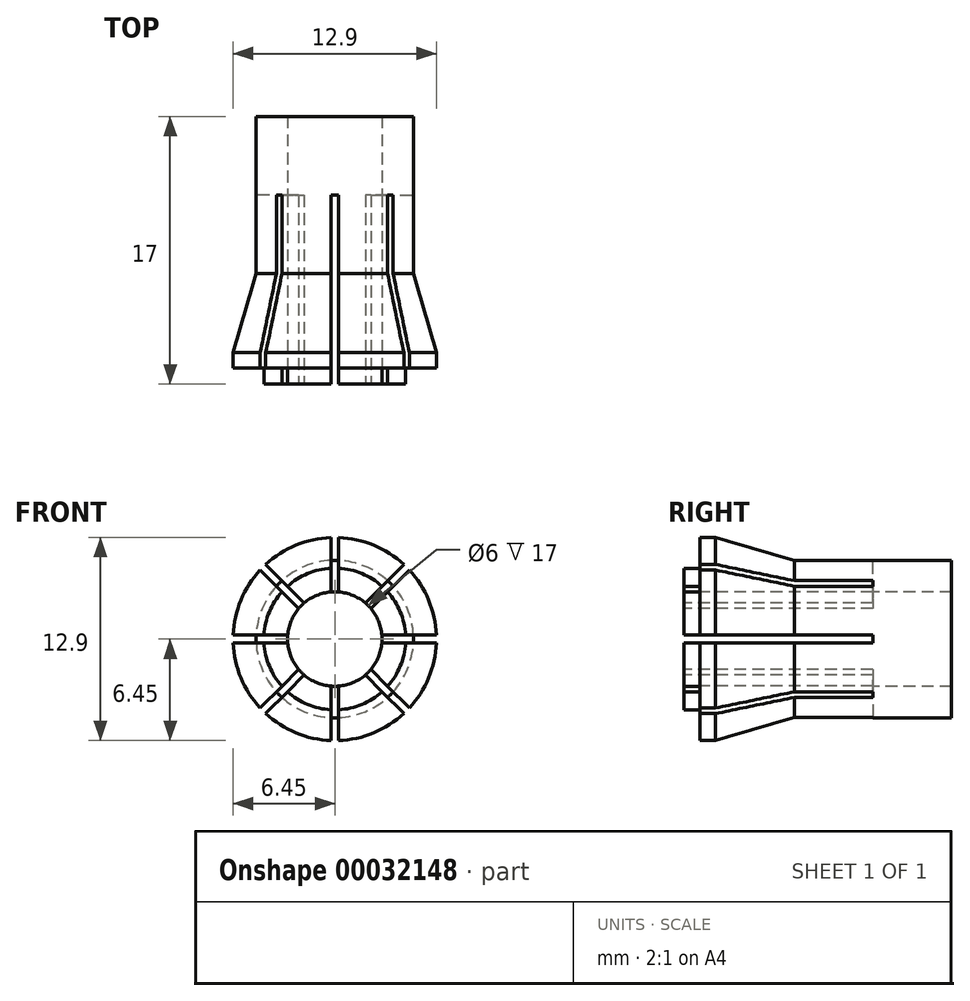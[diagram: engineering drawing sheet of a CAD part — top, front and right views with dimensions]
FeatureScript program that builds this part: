
annotation { "Feature Type Name" : "Feature", "Feature Type Description" : "" }
export const myFeature = defineFeature(function(context is Context, id is Id, definition is map)
    precondition{}
    {
        {
            var Q0;
            Q0=qCreatedBy(makeId("Right.planeOp"),FACE);
            var sketch = newSketch(context, id + "F0", { "sketchPlane" : qUnion([Q0])});
            skLineSegment(sketch, "E0", {"start": v(0, 5) * mm, "end": v(-10, 5) * mm});
            skLineSegment(sketch, "E1", {"start": v(-10, 5) * mm, "end": v(-15, 6.45) * mm});
            skLineSegment(sketch, "E2", {"start": v(-15, 6.45) * mm, "end": v(-16, 6.45) * mm});
            skLineSegment(sketch, "E3", {"start": v(-16, 6.45) * mm, "end": v(-16, 4.5) * mm});
            skLineSegment(sketch, "E4", {"start": v(-16, 4.5) * mm, "end": v(-17, 4.5) * mm});
            skLineSegment(sketch, "E5", {"start": v(-17, 4.5) * mm, "end": v(-17, 3) * mm});
            skLineSegment(sketch, "E6", {"start": v(-17, 0) * mm, "end": v(0, 0) * mm});
            skLineSegment(sketch, "E7.0", {"start": v(-17, 3) * mm, "end": v(0, 3) * mm});
            skLineSegment(sketch, "E8", {"start": v(0, 5) * mm, "end": v(0, 3) * mm});
            skPoint(sketch, "E9.orphan", {"position": v(-23.9, 0) * mm});
            skSolve(sketch);
        }
        {
            var Q0;
            Q0 = qSketchRegion(id + "F0", true);
            var Q1;
            Q1=sQuery(id+"F0.wireOp",EDGE,"E6");
            revolve(context, id + "F1", {"entities" : qUnion([Q0]), "axis" : qUnion([Q1]), "revolveType" : RevolveType.FULL});
        }
        {
            var Q0;
            Q0=makeQuery(id+"F1.opRevolve","SWEPT_FACE",FACE,{"disambiguationData":[OSD([sQuery(id+"F0.wireOp",EDGE,"E5")])]});
            var sketch = newSketch(context, id + "F2", { "sketchPlane" : qUnion([Q0])});
            skLineSegment(sketch, "E10", {"start": v(-0.25, 0) * mm, "end": v(-0.25, 6.5) * mm});
            skLineSegment(sketch, "E11", {"start": v(-0.25, 6.5) * mm, "end": v(0.25, 6.5) * mm});
            skLineSegment(sketch, "E12", {"start": v(0.25, 6.5) * mm, "end": v(0.25, 0) * mm});
            skLineSegment(sketch, "E13", {"start": v(-0.25, 0) * mm, "end": v(0.25, 0) * mm});
            skLineSegment(sketch, "E14.1.0", {"start": v(-0.18, -0.18) * mm, "end": v(-4.77, 4.42) * mm});
            skLineSegment(sketch, "E14.1.1", {"start": v(-4.42, 4.77) * mm, "end": v(0.18, 0.18) * mm});
            skLineSegment(sketch, "E14.1.2", {"start": v(-4.77, 4.42) * mm, "end": v(-4.42, 4.77) * mm});
            skLineSegment(sketch, "E14.1.3", {"start": v(-0.18, -0.18) * mm, "end": v(0.18, 0.18) * mm});
            skLineSegment(sketch, "E14.1.4", {"start": v(-0.18, -0.18) * mm, "end": v(0.18, 0.18) * mm});
            skLineSegment(sketch, "E14.2.0", {"start": v(0, -0.25) * mm, "end": v(-6.5, -0.25) * mm});
            skLineSegment(sketch, "E14.2.1", {"start": v(-6.5, 0.25) * mm, "end": v(0, 0.25) * mm});
            skLineSegment(sketch, "E14.2.2", {"start": v(-6.5, -0.25) * mm, "end": v(-6.5, 0.25) * mm});
            skLineSegment(sketch, "E14.2.3", {"start": v(0, -0.25) * mm, "end": v(0, 0.25) * mm});
            skLineSegment(sketch, "E14.2.4", {"start": v(0, -0.25) * mm, "end": v(0, 0.25) * mm});
            skLineSegment(sketch, "E14.3.0", {"start": v(0.18, -0.18) * mm, "end": v(-4.42, -4.77) * mm});
            skLineSegment(sketch, "E14.3.1", {"start": v(-4.77, -4.42) * mm, "end": v(-0.18, 0.18) * mm});
            skLineSegment(sketch, "E14.3.2", {"start": v(-4.42, -4.77) * mm, "end": v(-4.77, -4.42) * mm});
            skLineSegment(sketch, "E14.3.3", {"start": v(0.18, -0.18) * mm, "end": v(-0.18, 0.18) * mm});
            skLineSegment(sketch, "E14.3.4", {"start": v(0.18, -0.18) * mm, "end": v(-0.18, 0.18) * mm});
            skLineSegment(sketch, "E14.4.0", {"start": v(0.25, 0) * mm, "end": v(0.25, -6.5) * mm});
            skLineSegment(sketch, "E14.4.1", {"start": v(-0.25, -6.5) * mm, "end": v(-0.25, 0) * mm});
            skLineSegment(sketch, "E14.4.2", {"start": v(0.25, -6.5) * mm, "end": v(-0.25, -6.5) * mm});
            skLineSegment(sketch, "E14.4.3", {"start": v(0.25, 0) * mm, "end": v(-0.25, 0) * mm});
            skLineSegment(sketch, "E14.4.4", {"start": v(0.25, 0) * mm, "end": v(-0.25, 0) * mm});
            skLineSegment(sketch, "E14.5.0", {"start": v(0.18, 0.18) * mm, "end": v(4.77, -4.42) * mm});
            skLineSegment(sketch, "E14.5.1", {"start": v(4.42, -4.77) * mm, "end": v(-0.18, -0.18) * mm});
            skLineSegment(sketch, "E14.5.2", {"start": v(4.77, -4.42) * mm, "end": v(4.42, -4.77) * mm});
            skLineSegment(sketch, "E14.5.3", {"start": v(0.18, 0.18) * mm, "end": v(-0.18, -0.18) * mm});
            skLineSegment(sketch, "E14.5.4", {"start": v(0.18, 0.18) * mm, "end": v(-0.18, -0.18) * mm});
            skLineSegment(sketch, "E14.6.0", {"start": v(0, 0.25) * mm, "end": v(6.5, 0.25) * mm});
            skLineSegment(sketch, "E14.6.1", {"start": v(6.5, -0.25) * mm, "end": v(0, -0.25) * mm});
            skLineSegment(sketch, "E14.6.2", {"start": v(6.5, 0.25) * mm, "end": v(6.5, -0.25) * mm});
            skLineSegment(sketch, "E14.6.3", {"start": v(0, 0.25) * mm, "end": v(0, -0.25) * mm});
            skLineSegment(sketch, "E14.6.4", {"start": v(0, 0.25) * mm, "end": v(0, -0.25) * mm});
            skLineSegment(sketch, "E14.7.0", {"start": v(-0.18, 0.18) * mm, "end": v(4.42, 4.77) * mm});
            skLineSegment(sketch, "E14.7.1", {"start": v(4.77, 4.42) * mm, "end": v(0.18, -0.18) * mm});
            skLineSegment(sketch, "E14.7.2", {"start": v(4.42, 4.77) * mm, "end": v(4.77, 4.42) * mm});
            skLineSegment(sketch, "E14.7.3", {"start": v(-0.18, 0.18) * mm, "end": v(0.18, -0.18) * mm});
            skLineSegment(sketch, "E14.7.4", {"start": v(-0.18, 0.18) * mm, "end": v(0.18, -0.18) * mm});
            skPoint(sketch, "E14.center", {"position": v(0, 0) * mm});
            skSolve(sketch);
        }
        {
            var Q0;
            Q0 = qSketchRegion(id + "F2", true);
            extrude(context, id + "F3", {"entities" : qUnion([Q0]), "operationType" : NewBodyOperationType.REMOVE, "oppositeDirection" : true, "depth" : 12 * mm});
        }
    });
